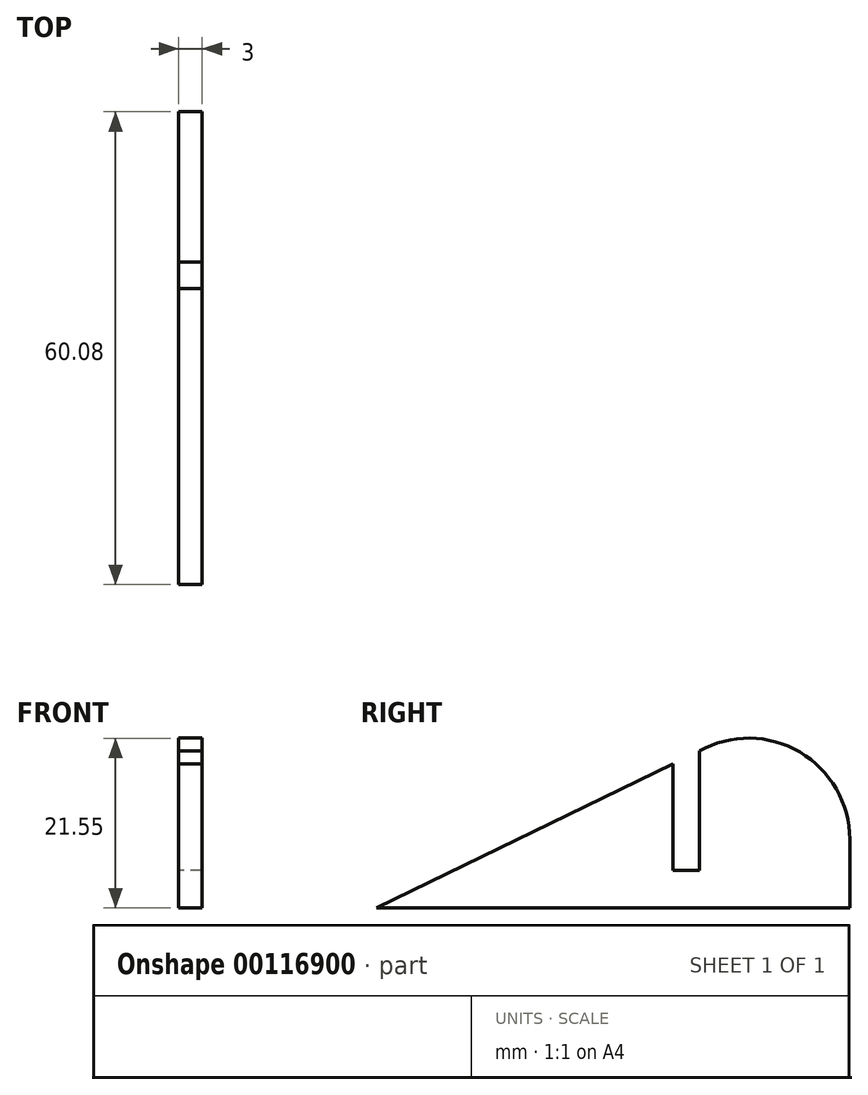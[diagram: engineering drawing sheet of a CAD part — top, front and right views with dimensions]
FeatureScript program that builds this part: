
annotation { "Feature Type Name" : "Feature", "Feature Type Description" : "" }
export const myFeature = defineFeature(function(context is Context, id is Id, definition is map)
    precondition{}
    {
        {
            var Q0;
            Q0=qCreatedBy(makeId("Right.planeOp"),FACE);
            var sketch = newSketch(context, id + "F0", { "sketchPlane" : qUnion([Q0])});
            skLineSegment(sketch, "E0", {"start": v(55.03, -29.06) * mm, "end": v(-5.05, -29.06) * mm});
            skLineSegment(sketch, "E1", {"start": v(55.03, -29.06) * mm, "end": v(55.03, -20.35) * mm});
            skArc(sketch, "E2", {"start": v(55.03, -20.35) * mm, "mid": v(48.7, -9.28) * mm, "end": v(35.94, -9.12) * mm});
            skLineSegment(sketch, "E3", {"start": v(32.57, -10.76) * mm, "end": v(-5.05, -29.06) * mm});
            skLineSegment(sketch, "E4", {"start": v(35.94, -9.12) * mm, "end": v(35.94, -24.28) * mm});
            skLineSegment(sketch, "E5", {"start": v(35.94, -24.28) * mm, "end": v(32.57, -24.28) * mm});
            skLineSegment(sketch, "E6", {"start": v(32.57, -24.28) * mm, "end": v(32.57, -10.76) * mm});
            skSolve(sketch);
        }
        {
            var Q0;
            Q0 = qSketchRegion(id + "F0", true);
            extrude(context, id + "F1", {"entities" : qUnion([Q0]), "depth" : 3 * mm});
        }
    });
